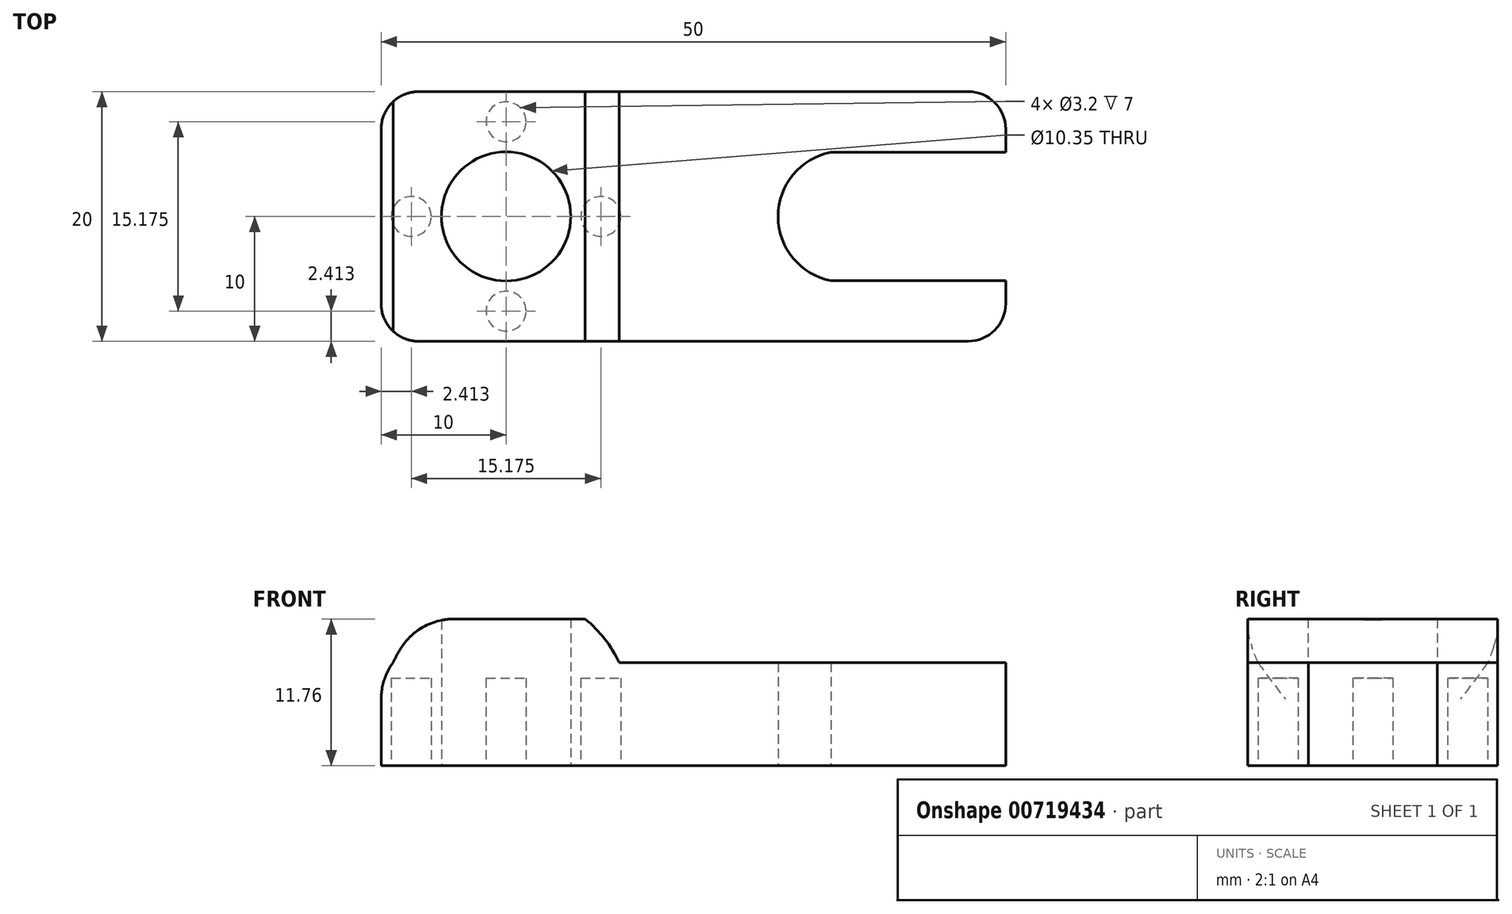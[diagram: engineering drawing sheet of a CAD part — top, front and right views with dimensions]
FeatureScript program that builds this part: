
annotation { "Feature Type Name" : "Feature", "Feature Type Description" : "" }
export const myFeature = defineFeature(function(context is Context, id is Id, definition is map)
    precondition{}
    {
        {
            var Q0;
            Q0=qCreatedBy(makeId("Front.planeOp"),FACE);
            var sketch = newSketch(context, id + "F0", { "sketchPlane" : qUnion([Q0])});
            skLineSegment(sketch, "E0.bottom", {"start": v(25, -4.12) * mm, "end": v(-25, -4.13) * mm});
            skLineSegment(sketch, "E0.top", {"start": v(25, 4.13) * mm, "end": v(-5.94, 4.12) * mm});
            skLineSegment(sketch, "E0.left", {"start": v(25, -4.13) * mm, "end": v(25, 4.13) * mm});
            skLineSegment(sketch, "E0.right", {"start": v(-25, -4.13) * mm, "end": v(-25, 4.12) * mm});
            skPoint(sketch, "E0.middle", {"position": v(0, 0) * mm});
            skArc(sketch, "E1", {"start": v(-5.94, 4.12) * mm, "mid": v(-15, 9.89) * mm, "end": v(-24.06, 4.12) * mm});
            skLineSegment(sketch, "E2.trimOffspring", {"start": v(-24.06, 4.12) * mm, "end": v(-25, 4.12) * mm});
            skSolve(sketch);
        }
        {
            var Q0;
            Q0=makeQuery(id+"F0.imprint","IMPRINT",FACE,{"disambiguationData":[TD([[makeQuery(id+"F0.imprint","IMPRINT",EDGE,{"derivedFrom":sQuery(id+"F0.wireOp",EDGE,"E0.bottom")}),-1.0]])]});
            extrude(context, id + "F1", {"entities" : qUnion([Q0]), "depth" : 20 * mm, "offsetDistance" : 25 * mm});
        }
        {
            var Q0;
            Q0=makeQuery(id+"F1.opExtrude","SWEPT_FACE",FACE,{"disambiguationData":[OSD([sQuery(id+"F0.wireOp",EDGE,"E0.bottom")])]});
            var sketch = newSketch(context, id + "F2", { "sketchPlane" : qUnion([Q0])});
            skCircle(sketch, "E3", {"center": v(-15, 10) * mm, "radius": 10 * mm});
            skCircle(sketch, "E4", {"center": v(-15, 10) * mm, "radius": 5.17 * mm});
            skCircle(sketch, "E5", {"center": v(-15, 17.59) * mm, "radius": 1.6 * mm});
            skCircle(sketch, "E6", {"center": v(-7.41, 10) * mm, "radius": 1.6 * mm});
            skCircle(sketch, "E7", {"center": v(-15, 2.41) * mm, "radius": 1.6 * mm});
            skCircle(sketch, "E8", {"center": v(-22.59, 10) * mm, "radius": 1.6 * mm});
            skPoint(sketch, "E9.orphan", {"position": v(-15, 20) * mm});
            skPoint(sketch, "E10.start.orphan", {"position": v(-15, 15.18) * mm});
            skPoint(sketch, "E11.trimOffspring.start.orphan", {"position": v(-15, 4.83) * mm});
            skPoint(sketch, "E12.trimOffspring.end.orphan", {"position": v(-15, 0) * mm});
            skPoint(sketch, "E13.orphan", {"position": v(-9.83, 10) * mm});
            skPoint(sketch, "E14.end.orphan", {"position": v(-5, 10) * mm});
            skPoint(sketch, "E15.orphan", {"position": v(-25, 10) * mm});
            skPoint(sketch, "E16.trimOffspring.start.orphan", {"position": v(-20.18, 10) * mm});
            skLineSegment(sketch, "E17", {"start": v(-25, 10) * mm, "end": v(59.71, 10) * mm, "construction": true});
            skLineSegment(sketch, "E18", {"start": v(-9.83, 10) * mm, "end": v(-9.83, -16.35) * mm, "construction": true});
            skLineSegment(sketch, "E19.0", {"start": v(12.02, 10) * mm, "end": v(12.02, -16.35) * mm, "construction": true});
            skLineSegment(sketch, "E20", {"start": v(25, 15.15) * mm, "end": v(25, 4.85) * mm});
            skLineSegment(sketch, "E21.0", {"start": v(11.02, 4.85) * mm, "end": v(25, 4.85) * mm});
            skLineSegment(sketch, "E22.MirrorCS", {"start": v(11.02, 15.15) * mm, "end": v(25, 15.15) * mm});
            skArc(sketch, "E23.trimOffspring", {"start": v(11.02, 15.15) * mm, "mid": v(6.77, 10) * mm, "end": v(11.02, 4.85) * mm});
            skSolve(sketch);
        }
        {
            var Q0;
            Q0=makeQuery(id+"F2.imprint","IMPRINT",FACE,{"disambiguationData":[TD([[makeQuery(id+"F2.imprint","IMPRINT",EDGE,{"derivedFrom":sQuery(id+"F2.wireOp",EDGE,"JHpM7IRo-5FgN-sgKf-JrOU-X9JCUNcVyaxe")}),1.0]])]});
            var Q1;
            Q1=makeQuery(id+"F2.imprint","IMPRINT",FACE,{"disambiguationData":[TD([[makeQuery(id+"F2.imprint","IMPRINT",EDGE,{"derivedFrom":sQuery(id+"F2.wireOp",EDGE,"E8")}),1.0]])]});
            var Q2;
            Q2=makeQuery(id+"F2.imprint","IMPRINT",FACE,{"disambiguationData":[TD([[makeQuery(id+"F2.imprint","IMPRINT",EDGE,{"derivedFrom":sQuery(id+"F2.wireOp",EDGE,"E4")}),1.0]])]});
            var Q3;
            Q3=makeQuery(id+"F2.imprint","IMPRINT",FACE,{"disambiguationData":[TD([[makeQuery(id+"F2.imprint","IMPRINT",EDGE,{"derivedFrom":sQuery(id+"F2.wireOp",EDGE,"E5")}),1.0]])]});
            var Q4;
            Q4=makeQuery(id+"F2.imprint","IMPRINT",FACE,{"disambiguationData":[TD([[makeQuery(id+"F2.imprint","IMPRINT",EDGE,{"derivedFrom":sQuery(id+"F2.wireOp",EDGE,"E7")}),1.0]])]});
            var Q5;
            Q5=makeQuery(id+"F2.imprint","IMPRINT",FACE,{"disambiguationData":[TD([[makeQuery(id+"F2.imprint","IMPRINT",EDGE,{"derivedFrom":sQuery(id+"F2.wireOp",EDGE,"E6")}),1.0]])]});
            extrude(context, id + "F3", {"entities" : qUnion([Q0, Q1, Q2, Q3, Q4, Q5]), "operationType" : NewBodyOperationType.REMOVE, "oppositeDirection" : true, "depth" : 7 * mm, "offsetDistance" : 25 * mm});
        }
        {
            var Q0;
            Q0=makeQuery(id+"F3.boolean.opBoolean","COPY",FACE,{"derivedFrom":makeQuery(id+"F3.opExtrude","CAP_FACE",FACE,{"disambiguationData":[OSD([sQuery(id+"F2.wireOp",EDGE,"E4")])],"isStart":false})});
            extrude(context, id + "F4", {"entities" : qUnion([Q0]), "operationType" : NewBodyOperationType.REMOVE, "oppositeDirection" : true, "depth" : 25 * mm, "offsetDistance" : 25 * mm});
        }
        {
            var Q0;
            Q0=makeQuery(id+"F1.opExtrude","CAP_EDGE",EDGE,{"disambiguationData":[OSD([sQuery(id+"F0.wireOp",EDGE,"E0.left")])],"isStart":true});
            var Q1;
            Q1=makeQuery(id+"F1.opExtrude","CAP_EDGE",EDGE,{"disambiguationData":[OSD([sQuery(id+"F0.wireOp",EDGE,"E0.left")])],"isStart":false});
            var Q2;
            Q2=makeQuery(id+"F1.opExtrude","CAP_EDGE",EDGE,{"disambiguationData":[OSD([sQuery(id+"F0.wireOp",EDGE,"E0.right")])],"isStart":true});
            var Q3;
            Q3=makeQuery(id+"F1.opExtrude","CAP_EDGE",EDGE,{"disambiguationData":[OSD([sQuery(id+"F0.wireOp",EDGE,"E0.right")])],"isStart":false});
            fillet(context, id + "F5", {"entities" : qUnion([Q0, Q1, Q2, Q3]), "radius" : 3 * mm, "tangentPropagation" : true, "defaultsChanged" : true, "vertexSettings" : [], "allowEdgeOverflow" : false});
        }
        {
            var Q0;
            Q0=makeQuery(id+"F1.opExtrude","SWEPT_EDGE",EDGE,{"disambiguationData":[OSD([sQuery(id+"F0.wireOp",EDGE,"E0.right"),sQuery(id+"F0.wireOp",EDGE,"E2.trimOffspring")])]});
            fillet(context, id + "F6", {"entities" : qUnion([Q0]), "radius" : 5 * mm, "tangentPropagation" : true, "allowEdgeOverflow" : false});
        }
        {
            var Q0;
            Q0=makeQuery(id+"F2.imprint","IMPRINT",FACE,{"disambiguationData":[TD([[makeQuery(id+"F2.imprint","IMPRINT",EDGE,{"derivedFrom":sQuery(id+"F2.wireOp",EDGE,"E20")}),-1.0]])]});
            extrude(context, id + "F7", {"entities" : qUnion([Q0]), "operationType" : NewBodyOperationType.REMOVE, "oppositeDirection" : true, "depth" : 25 * mm, "offsetDistance" : 25 * mm});
        }
        {
            var Q0;
            Q0=makeQuery(id+"F1.opExtrude","CAP_FACE",FACE,{"disambiguationData":[OSD([sQuery(id+"F0.wireOp",EDGE,"E0.bottom"),sQuery(id+"F0.wireOp",EDGE,"E0.top"),sQuery(id+"F0.wireOp",EDGE,"E0.left"),sQuery(id+"F0.wireOp",EDGE,"E0.right"),sQuery(id+"F0.wireOp",EDGE,"E1"),sQuery(id+"F0.wireOp",EDGE,"E2.trimOffspring")])],"isStart":false});
            var sketch = newSketch(context, id + "F8", { "sketchPlane" : qUnion([Q0])});
            skLineSegment(sketch, "E24.0", {"start": v(-5.94, 7.62) * mm, "end": v(-39.55, 7.62) * mm});
            skSolve(sketch);
        }
        {
            var Q0;
            {var subQ0=sQuery(id+"F8.wireOp",EDGE,"E24.0");var subQ1=makeQuery(id+"F1.opExtrude","CAP_EDGE",EDGE,{"disambiguationData":[OSD([sQuery(id+"F0.wireOp",EDGE,"E1")])],"isStart":false});var subQ2=makeQuery(id+"F8.imprint","INTERSECT",VERTEX,{"disambiguationData":[OD(0.0)],"derivedFrom":[subQ1,subQ0]});Q0=makeQuery(id+"F8.imprint","IMPRINT",FACE,{"disambiguationData":[TD([[makeQuery(id+"F8.imprint","IMPRINT",EDGE,{"disambiguationData":[TD([[subQ2,-1.0]])],"derivedFrom":subQ0}),-1.0]])]});}
            extrude(context, id + "F9", {"entities" : qUnion([Q0]), "operationType" : NewBodyOperationType.REMOVE, "oppositeDirection" : true, "depth" : 25 * mm, "offsetDistance" : 25 * mm});
        }
        {
            var Q0;
            {var subQ0=sQuery(id+"F8.wireOp",EDGE,"E24.0");var subQ1=sQuery(id+"F0.wireOp",EDGE,"E1");Q0=makeQuery(id+"F9.boolean.opBoolean","COPY",EDGE,{"derivedFrom":makeQuery(id+"F9.opExtrude","SWEPT_EDGE",EDGE,{"disambiguationData":[OSD([subQ1,subQ0]),TDD([makeQuery(id+"F8.imprint","INTERSECT",VERTEX,{"disambiguationData":[OD(1.0)],"derivedFrom":[makeQuery(id+"F1.opExtrude","CAP_EDGE",EDGE,{"disambiguationData":[OSD([subQ1])],"isStart":false}),subQ0]})])]})});}
            var Q1;
            {var subQ0=sQuery(id+"F8.wireOp",EDGE,"E24.0");var subQ1=sQuery(id+"F0.wireOp",EDGE,"E1");Q1=makeQuery(id+"F9.boolean.opBoolean","COPY",EDGE,{"derivedFrom":makeQuery(id+"F9.opExtrude","SWEPT_EDGE",EDGE,{"disambiguationData":[OSD([subQ1,subQ0]),TDD([makeQuery(id+"F8.imprint","INTERSECT",VERTEX,{"disambiguationData":[OD(0.0)],"derivedFrom":[makeQuery(id+"F1.opExtrude","CAP_EDGE",EDGE,{"disambiguationData":[OSD([subQ1])],"isStart":false}),subQ0]})])]})});}
            fillet(context, id + "F10", {"entities" : qUnion([Q0, Q1]), "tangentPropagation" : true, "radius" : 5 * mm, "defaultsChanged" : false, "vertexSettings" : [], "allowEdgeOverflow" : false});
        }
    });
